# Revit family: Building-Materials_Glass-Glazing_Vitro-Architectural-Glass_Interior-Starphire-Glass
name_source: partatom
category: Curtain Panels
units: mm (PartAtom-declared; Revit-internal decimal feet)

## family parameters
Always vertical = Yes
Classification Number = 23.25.20.14.11.11.17
Cut with Voids When Loaded = No
Shared = No

## types (9) — shared parameters
Analytic Construction = Large single-glazed windows
Assembly Code = B2020220
Define Thermal Properties by = Schematic Type
Description = The unique Starphire® glass edge brings more light into interior spaces while offering unmatched levels of brightness, color fidelity, clarity and visual excitement.
Finish = Glass
Glass Material = Vitro Architectural-Glass - Starphire
Heat Transfer Coefficient (U) = 0.29 BTU/(h·ft²·°F)
Keynote = 08900
Manufacturer = Vitro Architectural Glass
Product Guid = 72ebaecd-b86f-4219-9226-cf644da1d110
Product Page URL = https://www.vitroglazings.com
Product data url = https://www.bimobject.com
Reflectance (Visible Exterior) = 8
Reflectance (Visible Interior) = 8
Thermal Resistance (R) = 8.3333 (h·ft²·°F)/BTU
URL = https://www.vitroglazings.com
zero-valued in all types: U-Value Argon (Summer Day), U-Value Argon (Winter Night)

## per-type parameters (varying)
| type | ISO Damage Weighted Transmittance | Light to Solar Gain | Shadow Coefficient | Solar Heat Gain Coefficient | Solar Light Transmittance | Thickness | U-Value Air (Summer Day) | U-Value Air (Winter Night) | UV Light Transmittance | Visual Light Transmittance |
| Starphire for Interiors 1/8" | 0 | 1 | 0 | 0.91 | 0.9 | 0' - 0 1/8" | 0 BTU/(h·ft²·°F) | 1.04 BTU/(h·ft²·°F) | 0.89 | 0.91 |
| Starphire for Interiors 5/32" | 0 | 1 | 0 | 0.91 | 0.9 | 0' - 0 5/32" | 0 BTU/(h·ft²·°F) | 1.04 BTU/(h·ft²·°F) | 0.88 | 0.91 |
| Starphire for Interiors 3/16" | 0 | 1.01 | 0 | 0.9 | 0.9 | 0' - 0 3/16" | 0 BTU/(h·ft²·°F) | 1.03 BTU/(h·ft²·°F) | 0.88 | 0.91 |
| Starphire for Interiors 1/4" | 0.898 | 1.01 | 1.03 | 0.9 | 0.89 | 0' - 0 1/4" | 0.92 BTU/(h·ft²·°F) | 1.02 BTU/(h·ft²·°F) | 0.87 | 0.91 |
| Starphire for Interiors 5/16" | 0 | 1.02 | 0 | 0.89 | 0.88 | 0' - 0 5/16" | 0 BTU/(h·ft²·°F) | 1.01 BTU/(h·ft²·°F) | 0.86 | 0.91 |
| Starphire for Interiors 3/8" | 0 | 1.02 | 0 | 0.89 | 0.87 | 0' - 0 3/8" | 0 BTU/(h·ft²·°F) | 1 BTU/(h·ft²·°F) | 0.85 | 0.91 |
| Starphire for Interiors 1/2" | 0 | 1.02 | 0 | 0.88 | 0.86 | 0' - 0 1/2" | 0 BTU/(h·ft²·°F) | 0.98 BTU/(h·ft²·°F) | 0.83 | 0.9 |
| Starphire for Interiors 5/8" | 0 | 1.03 | 0 | 0.87 | 0.84 | 0' - 0 5/8" | 0 BTU/(h·ft²·°F) | 0.97 BTU/(h·ft²·°F) | 0.81 | 0.9 |
| Starphire for Interiors 3/4" | 0 | 1.05 | 0 | 0.86 | 0.83 | 0' - 0 3/4" | 0 BTU/(h·ft²·°F) | 0.95 BTU/(h·ft²·°F) | 0.8 | 0.9 |

note: column(s) folded — value = type name in every type: Model

## geometry (parser evidence)
native form markers: Sweep x2
no freeform markers — native parametric forms only
